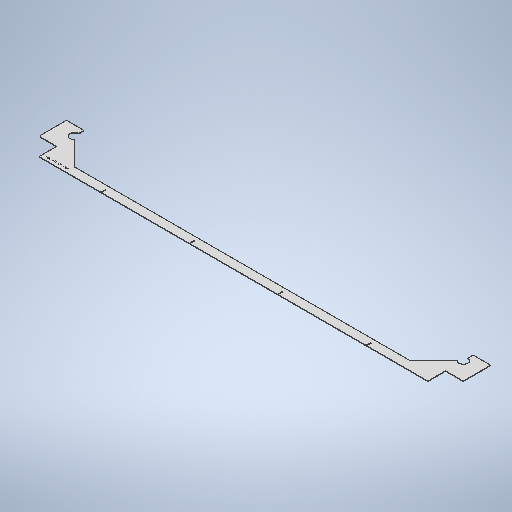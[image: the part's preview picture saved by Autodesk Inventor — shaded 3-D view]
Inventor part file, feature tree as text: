
AUTODESK INVENTOR PART (.ipt)
format: ipt  version: 2025 (Build 290162010, 162A)  size: 440,320 bytes
history: native  units: mm
features: other x4, sketch x3, sheet_metal_op x1, extrude x1, mirror x1, pattern_linear x1
ambient origin geometry x8: Origin, YZ Plane, XZ Plane, XY Plane, X Axis, Y Axis, Z Axis, Center Point
bodies: Solid1 (feature_tree)
feature tree (11):
  sheet_metal_op  "Face1"
  extrude  "Extrusion1"  Depth=3.2mm
  mirror  "Mirror2"
  pattern_linear  "Rectangular Pattern3"  Spacing1=748.5mm  [1 undecoded]
  other  "Corner Chamfer1"
  other  "Mark1"
  sketch  "Sketch1"  dims[d2=3.0mm]
  other  "Plate1"
  sketch  "Sketch2"  dims[d3=2400.0mm d4=2900.0mm d5=50.0mm d6=100.0mm d7=50.0mm d8=2644.536997mm d9=135.0deg d10=949.536997mm d11=1149.536997mm d12=23.747141mm d13=50.0mm d14=100.0mm d15=212.786819mm d16=2700.0mm d17=55.0mm d18=200.0mm d19=200.0mm d20=3.2mm]
  sketch  "Sketch3"  dims[d21=26.0mm d22=748.5mm d23=0.0mm d24=0.0mm d31=50.0mm d33=500.0mm d34=6.0mm d35=6.0mm d36=45.0deg]
  other  "Definition1"
note: 1 required parameter value undecoded (feature->parameter linkage not recoverable at this tier; creation-order binding heuristic only, values carry confidence <= 0.55)
